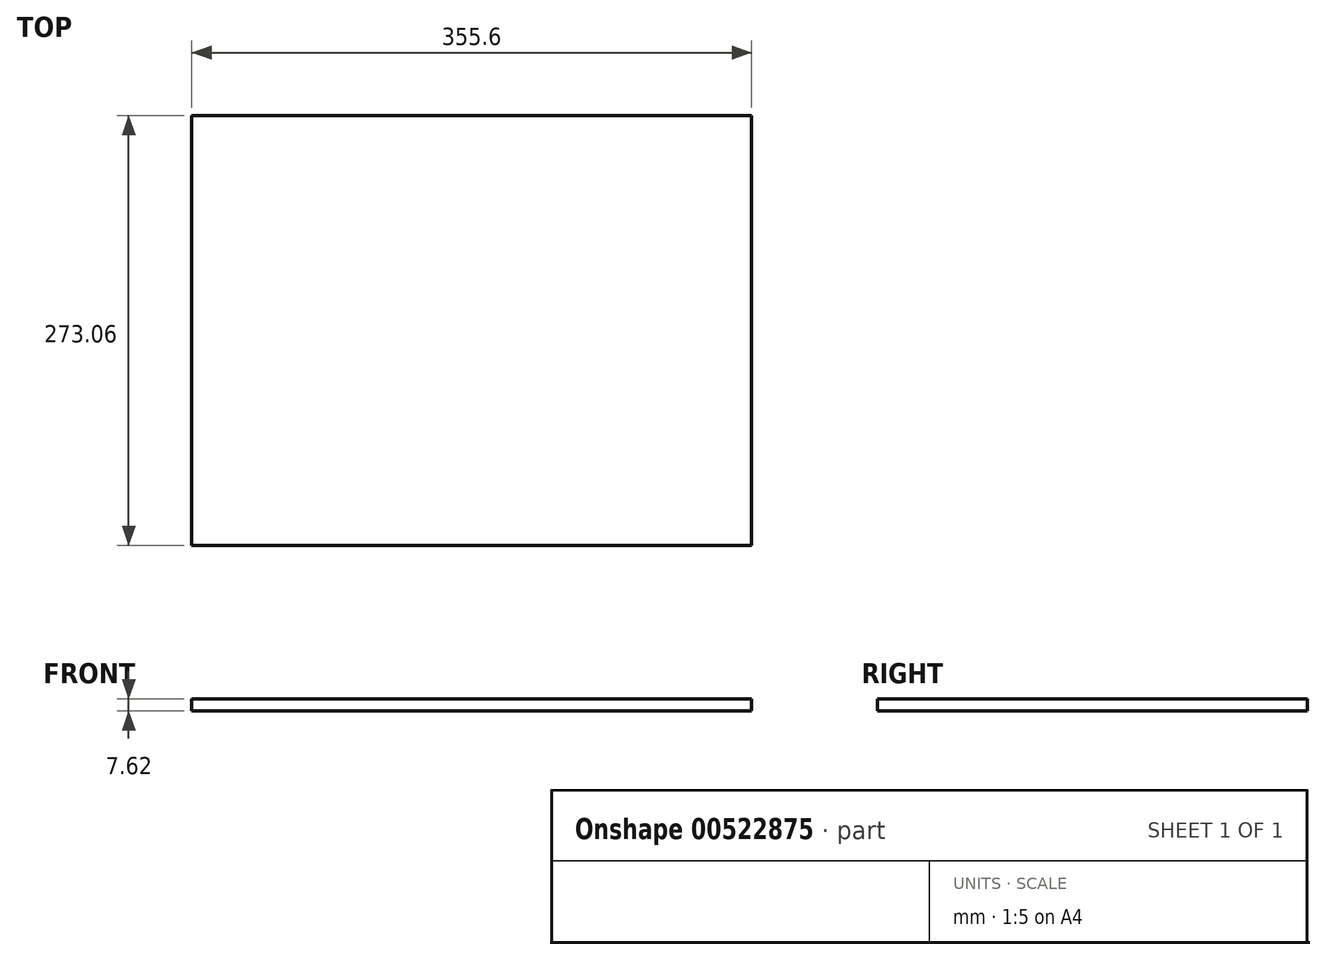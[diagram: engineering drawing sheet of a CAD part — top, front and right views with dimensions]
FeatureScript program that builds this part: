
annotation { "Feature Type Name" : "Feature", "Feature Type Description" : "" }
export const myFeature = defineFeature(function(context is Context, id is Id, definition is map)
    precondition{}
    {
        {
            var Q0;
            Q0=qCreatedBy(makeId("Top.planeOp"),FACE);
            var sketch = newSketch(context, id + "F0", { "sketchPlane" : qUnion([Q0])});
            skLineSegment(sketch, "E0.bottom", {"start": v(-177.8, 136.53) * mm, "end": v(177.8, 136.53) * mm});
            skLineSegment(sketch, "E0.top", {"start": v(-177.8, -136.53) * mm, "end": v(177.8, -136.53) * mm});
            skLineSegment(sketch, "E0.left", {"start": v(-177.8, 136.53) * mm, "end": v(-177.8, -136.53) * mm});
            skLineSegment(sketch, "E0.right", {"start": v(177.8, 136.53) * mm, "end": v(177.8, -136.53) * mm});
            skPoint(sketch, "E0.middle", {"position": v(0, 0) * mm});
            skSolve(sketch);
        }
        {
            var Q0;
            Q0=makeQuery(id+"F0.imprint","IMPRINT",FACE,{"disambiguationData":[TD([[makeQuery(id+"F0.imprint","IMPRINT",EDGE,{"derivedFrom":sQuery(id+"F0.wireOp",EDGE,"E0.bottom")}),-1.0]])]});
            extrude(context, id + "F1", {"entities" : qUnion([Q0]), "depth" : 7.62 * mm, "offsetDistance" : 25 * mm});
        }
    });
